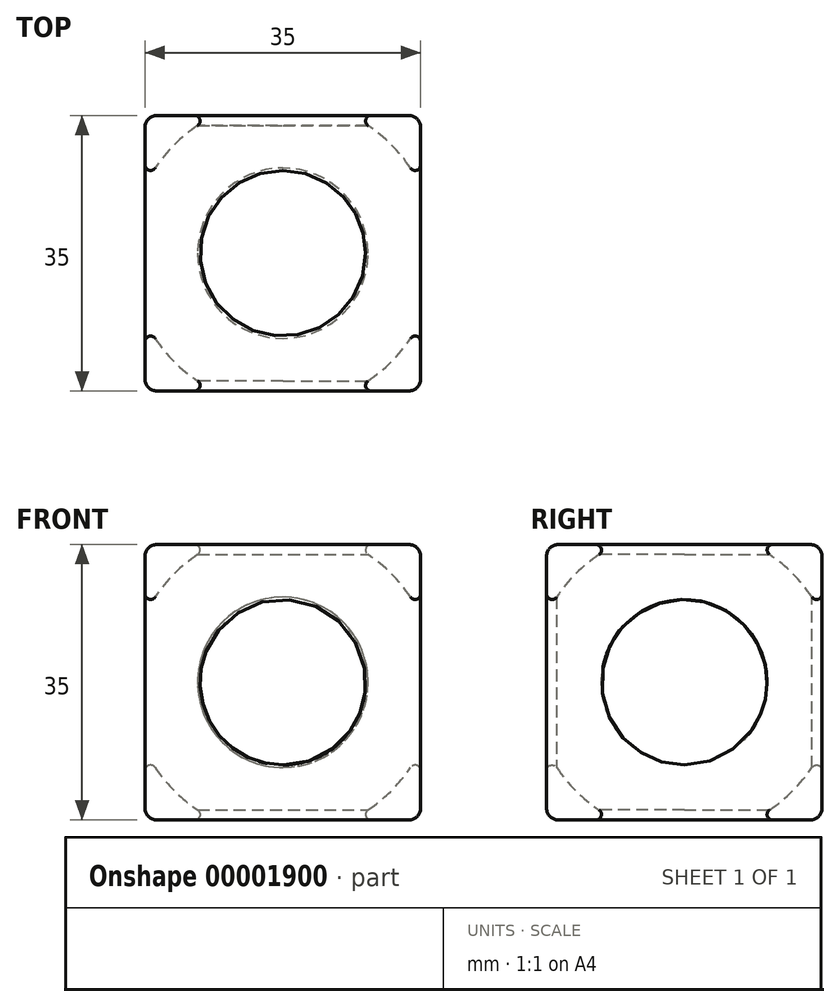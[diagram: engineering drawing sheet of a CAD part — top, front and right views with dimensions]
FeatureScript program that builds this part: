
annotation { "Feature Type Name" : "Feature", "Feature Type Description" : "" }
export const myFeature = defineFeature(function(context is Context, id is Id, definition is map)
    precondition{}
    {
        {
            var Q0;
            Q0=qCreatedBy(makeId("Top.planeOp"),FACE);
            var sketch = newSketch(context, id + "F0", { "sketchPlane" : qUnion([Q0])});
            skLineSegment(sketch, "E0.rect.bottom", {"start": v(10, 10) * mm, "end": v(-10, 10) * mm});
            skLineSegment(sketch, "E0.rect.top", {"start": v(10, -10) * mm, "end": v(-10, -10) * mm});
            skLineSegment(sketch, "E0.rect.left", {"start": v(10, 10) * mm, "end": v(10, -10) * mm});
            skLineSegment(sketch, "E0.rect.right", {"start": v(-10, 10) * mm, "end": v(-10, -10) * mm});
            skPoint(sketch, "E0.rect.middle", {"position": v(0, 0) * mm});
            skSolve(sketch);
        }
        {
            var Q0;
            Q0=qCreatedBy(makeId("Top.planeOp"),FACE);
            var sketch = newSketch(context, id + "F1", { "sketchPlane" : qUnion([Q0])});
            skArc(sketch, "E1", {"start": v(12, 0) * mm, "mid": v(0, 12) * mm, "end": v(-12, 0) * mm});
            skLineSegment(sketch, "E2", {"start": v(-12, 0) * mm, "end": v(12, 0) * mm});
            skSolve(sketch);
        }
        {
            var Q0;
            Q0=qCreatedBy(makeId("Top.planeOp"),FACE);
            var sketch = newSketch(context, id + "F2", { "sketchPlane" : qUnion([Q0])});
            skArc(sketch, "E3.0", {"start": v(14.8, 0) * mm, "mid": v(0, 14.8) * mm, "end": v(-14.8, 0) * mm});
            skArc(sketch, "E4.0", {"start": v(49.8, 0) * mm, "mid": v(0, 49.8) * mm, "end": v(-49.8, 0) * mm});
            skLineSegment(sketch, "E5", {"start": v(-49.8, 0) * mm, "end": v(-14.8, 0) * mm});
            skLineSegment(sketch, "E6", {"start": v(14.8, 0) * mm, "end": v(49.8, 0) * mm});
            skSolve(sketch);
        }
        {
            var Q0;
            Q0=makeQuery(id+"F0.imprint","IMPRINT",FACE,{"disambiguationData":[TD([[makeQuery(id+"F0.imprint","IMPRINT",EDGE,{"derivedFrom":sQuery(id+"F0.wireOp",EDGE,"E0.rect.bottom")}),1.0]])]});
            extrude(context, id + "F3", {"entities" : qUnion([Q0]), "endBound" : BoundingType.SYMMETRIC, "depth" : 20 * mm});
        }
        {
            var Q0;
            Q0=makeQuery(id+"F2.imprint","IMPRINT",FACE,{"disambiguationData":[TD([[makeQuery(id+"F2.imprint","IMPRINT",EDGE,{"derivedFrom":sQuery(id+"F2.wireOp",EDGE,"E3.0")}),-1.0]])]});
            var Q1;
            Q1=sQuery(id+"F2.wireOp",EDGE,"E5");
            revolve(context, id + "F4", {"operationType" : NewBodyOperationType.REMOVE, "entities" : qUnion([Q0]), "axis" : qUnion([Q1]), "revolveType" : RevolveType.FULL, "oppositeDirection" : true});
        }
        {
            var Q0;
            Q0=qSketchRegion(id+"F1",true);
            var Q1;
            Q1=sQuery(id+"F1.wireOp",EDGE,"E2");
            revolve(context, id + "F5", {"operationType" : NewBodyOperationType.REMOVE, "entities" : qUnion([Q0]), "axis" : qUnion([Q1]), "revolveType" : RevolveType.FULL, "oppositeDirection" : true});
        }
        {
            var Q0;
            Q0=qCreatedBy(makeId("Top.planeOp"),FACE);
            var sketch = newSketch(context, id + "F6", { "sketchPlane" : qUnion([Q0])});
            skArc(sketch, "E7.0", {"start": v(15.4, 0) * mm, "mid": v(0, 15.4) * mm, "end": v(-15.4, 0) * mm});
            skLineSegment(sketch, "E8", {"start": v(-15.4, 0) * mm, "end": v(15.4, 0) * mm});
            skLineSegment(sketch, "E9.rect.bottom", {"start": v(13.5, 13.5) * mm, "end": v(-13.5, 13.5) * mm});
            skLineSegment(sketch, "E9.rect.top", {"start": v(13.5, -13.5) * mm, "end": v(-13.5, -13.5) * mm});
            skLineSegment(sketch, "E9.rect.left", {"start": v(13.5, 13.5) * mm, "end": v(13.5, -13.5) * mm});
            skLineSegment(sketch, "E9.rect.right", {"start": v(-13.5, 13.5) * mm, "end": v(-13.5, -13.5) * mm});
            skArc(sketch, "E10.0", {"start": v(18.9, 0) * mm, "mid": v(0, 18.9) * mm, "end": v(-18.9, 0) * mm});
            skArc(sketch, "E11.0", {"start": v(33.9, 0) * mm, "mid": v(0, 33.9) * mm, "end": v(-33.9, 0) * mm});
            skLineSegment(sketch, "E12", {"start": v(-33.9, 0) * mm, "end": v(-18.9, 0) * mm});
            skLineSegment(sketch, "E13", {"start": v(18.9, 0) * mm, "end": v(33.9, 0) * mm});
            skSolve(sketch);
        }
        {
            var Q0;
            {var subQ1=sQuery(id+"F6.wireOp",EDGE,"E7.0");var subQ3=sQuery(id+"F6.wireOp",EDGE,"E9.rect.bottom");var subQ5=makeQuery(id+"F6.imprint","INTERSECT",VERTEX,{"disambiguationData":[OD(1.0)],"derivedFrom":[subQ1,subQ3]});Q0=makeQuery(id+"F6.imprint","IMPRINT",FACE,{"disambiguationData":[TD([[makeQuery(id+"F6.imprint","IMPRINT",EDGE,{"disambiguationData":[TD([[subQ5,-1.0]])],"derivedFrom":subQ1}),-1.0]])]});}
            var Q1;
            {var subQ3=sQuery(id+"F6.wireOp",EDGE,"E7.0");var subQ5=sQuery(id+"F6.wireOp",EDGE,"E9.rect.left");var subQ7=makeQuery(id+"F6.imprint","INTERSECT",VERTEX,{"derivedFrom":[subQ3,subQ5]});Q1=makeQuery(id+"F6.imprint","IMPRINT",FACE,{"disambiguationData":[TD([[makeQuery(id+"F6.imprint","IMPRINT",EDGE,{"disambiguationData":[TD([[subQ7,-1.0]])],"derivedFrom":subQ3}),1.0]])]});}
            var Q2;
            {var subQ0=sQuery(id+"F6.wireOp",EDGE,"E9.rect.left");var subQ1=sQuery(id+"F6.wireOp",EDGE,"E7.0");var subQ2=makeQuery(id+"F6.imprint","INTERSECT",VERTEX,{"derivedFrom":[subQ1,subQ0]});Q2=makeQuery(id+"F6.imprint","IMPRINT",FACE,{"disambiguationData":[TD([[makeQuery(id+"F6.imprint","IMPRINT",EDGE,{"disambiguationData":[TD([[subQ2,-1.0]])],"derivedFrom":subQ1}),-1.0]])]});}
            var Q3;
            {var subQ3=sQuery(id+"F6.wireOp",EDGE,"E9.rect.top");Q3=makeQuery(id+"F6.imprint","IMPRINT",FACE,{"disambiguationData":[TD([[makeQuery(id+"F6.imprint","IMPRINT",EDGE,{"derivedFrom":subQ3}),-1.0]])]});}
            var Q4;
            {var subQ0=sQuery(id+"F6.wireOp",EDGE,"E9.rect.left");var subQ3=sQuery(id+"F6.wireOp",EDGE,"E9.rect.bottom");var subQ4=makeQuery(id+"F6.imprint","INTERSECT",VERTEX,{"derivedFrom":[subQ3,subQ0]});Q4=makeQuery(id+"F6.imprint","IMPRINT",FACE,{"disambiguationData":[TD([[makeQuery(id+"F6.imprint","IMPRINT",EDGE,{"disambiguationData":[TD([[subQ4,-1.0]])],"derivedFrom":subQ3}),1.0]])]});}
            var Q5;
            {var subQ1=sQuery(id+"F6.wireOp",EDGE,"E9.rect.bottom");var subQ3=sQuery(id+"F6.wireOp",EDGE,"E9.rect.right");var subQ5=makeQuery(id+"F6.imprint","INTERSECT",VERTEX,{"derivedFrom":[subQ1,subQ3]});Q5=makeQuery(id+"F6.imprint","IMPRINT",FACE,{"disambiguationData":[TD([[makeQuery(id+"F6.imprint","IMPRINT",EDGE,{"disambiguationData":[TD([[subQ5,1.0]])],"derivedFrom":subQ1}),1.0]])]});}
            extrude(context, id + "F7", {"entities" : qUnion([Q0, Q1, Q2, Q3, Q4, Q5]), "endBound" : BoundingType.SYMMETRIC, "depth" : 27 * mm});
        }
        {
            var Q0;
            Q0=makeQuery(id+"F6.imprint","IMPRINT",FACE,{"disambiguationData":[TD([[makeQuery(id+"F6.imprint","IMPRINT",EDGE,{"derivedFrom":sQuery(id+"F6.wireOp",EDGE,"E11.0")}),1.0]])]});
            var Q1;
            {var subQ1=sQuery(id+"F6.wireOp",EDGE,"E9.rect.bottom");var subQ3=sQuery(id+"F6.wireOp",EDGE,"E9.rect.right");var subQ5=makeQuery(id+"F6.imprint","INTERSECT",VERTEX,{"derivedFrom":[subQ1,subQ3]});Q1=makeQuery(id+"F6.imprint","IMPRINT",FACE,{"disambiguationData":[TD([[makeQuery(id+"F6.imprint","IMPRINT",EDGE,{"disambiguationData":[TD([[subQ5,1.0]])],"derivedFrom":subQ1}),1.0]])]});}
            var Q2;
            {var subQ0=sQuery(id+"F6.wireOp",EDGE,"E9.rect.left");var subQ3=sQuery(id+"F6.wireOp",EDGE,"E9.rect.bottom");var subQ4=makeQuery(id+"F6.imprint","INTERSECT",VERTEX,{"derivedFrom":[subQ3,subQ0]});Q2=makeQuery(id+"F6.imprint","IMPRINT",FACE,{"disambiguationData":[TD([[makeQuery(id+"F6.imprint","IMPRINT",EDGE,{"disambiguationData":[TD([[subQ4,-1.0]])],"derivedFrom":subQ3}),1.0]])]});}
            var Q3;
            Q3=sQuery(id+"F6.wireOp",EDGE,"E12");
            revolve(context, id + "F8", {"operationType" : NewBodyOperationType.REMOVE, "entities" : qUnion([Q0, Q1, Q2]), "axis" : qUnion([Q3]), "revolveType" : RevolveType.FULL, "oppositeDirection" : true});
        }
        {
            var Q0;
            {var subQ1=sQuery(id+"F6.wireOp",EDGE,"E8");var subQ3=sQuery(id+"F6.wireOp",EDGE,"E7.0");var subQ5=makeQuery(id+"F6.imprint","INTERSECT",VERTEX,{"disambiguationData":[OD(1.0)],"derivedFrom":[subQ3,subQ1]});Q0=makeQuery(id+"F6.imprint","IMPRINT",FACE,{"disambiguationData":[TD([[makeQuery(id+"F6.imprint","IMPRINT",EDGE,{"disambiguationData":[TD([[subQ5,1.0]])],"derivedFrom":subQ3}),1.0]])]});}
            var Q1;
            {var subQ3=sQuery(id+"F6.wireOp",EDGE,"E7.0");var subQ5=sQuery(id+"F6.wireOp",EDGE,"E9.rect.left");var subQ7=makeQuery(id+"F6.imprint","INTERSECT",VERTEX,{"derivedFrom":[subQ3,subQ5]});Q1=makeQuery(id+"F6.imprint","IMPRINT",FACE,{"disambiguationData":[TD([[makeQuery(id+"F6.imprint","IMPRINT",EDGE,{"disambiguationData":[TD([[subQ7,-1.0]])],"derivedFrom":subQ3}),1.0]])]});}
            var Q2;
            {var subQ0=sQuery(id+"F6.wireOp",EDGE,"E9.rect.bottom");var subQ1=sQuery(id+"F6.wireOp",EDGE,"E7.0");var subQ3=makeQuery(id+"F6.imprint","INTERSECT",VERTEX,{"disambiguationData":[OD(0.0)],"derivedFrom":[subQ1,subQ0]});Q2=makeQuery(id+"F6.imprint","IMPRINT",FACE,{"disambiguationData":[TD([[makeQuery(id+"F6.imprint","IMPRINT",EDGE,{"disambiguationData":[TD([[subQ3,-1.0]])],"derivedFrom":subQ1}),1.0]])]});}
            var Q3;
            {var subQ1=sQuery(id+"F6.wireOp",EDGE,"E8");var subQ3=sQuery(id+"F6.wireOp",EDGE,"E7.0");var subQ5=makeQuery(id+"F6.imprint","INTERSECT",VERTEX,{"disambiguationData":[OD(0.0)],"derivedFrom":[subQ3,subQ1]});Q3=makeQuery(id+"F6.imprint","IMPRINT",FACE,{"disambiguationData":[TD([[makeQuery(id+"F6.imprint","IMPRINT",EDGE,{"disambiguationData":[TD([[subQ5,-1.0]])],"derivedFrom":subQ3}),1.0]])]});}
            var Q4;
            Q4=sQuery(id+"F6.wireOp",EDGE,"E8");
            revolve(context, id + "F9", {"operationType" : NewBodyOperationType.REMOVE, "entities" : qUnion([Q0, Q1, Q2, Q3]), "axis" : qUnion([Q4]), "revolveType" : RevolveType.FULL, "oppositeDirection" : true});
        }
        {
            var Q0;
            Q0=qCreatedBy(makeId("Top.planeOp"),FACE);
            var sketch = newSketch(context, id + "F10", { "sketchPlane" : qUnion([Q0])});
            skArc(sketch, "E14.0", {"start": v(19.5, 0) * mm, "mid": v(0, 19.5) * mm, "end": v(-19.5, 0) * mm});
            skLineSegment(sketch, "E15", {"start": v(-19.5, 0) * mm, "end": v(19.5, 0) * mm});
            skLineSegment(sketch, "E16.rect.bottom", {"start": v(17.5, 17.5) * mm, "end": v(-17.5, 17.5) * mm});
            skLineSegment(sketch, "E16.rect.top", {"start": v(17.5, -17.5) * mm, "end": v(-17.5, -17.5) * mm});
            skLineSegment(sketch, "E16.rect.left", {"start": v(17.5, 17.5) * mm, "end": v(17.5, -17.5) * mm});
            skLineSegment(sketch, "E16.rect.right", {"start": v(-17.5, 17.5) * mm, "end": v(-17.5, -17.5) * mm});
            skArc(sketch, "E17.0", {"start": v(23, 0) * mm, "mid": v(0, 23) * mm, "end": v(-23, 0) * mm});
            skArc(sketch, "E18.0", {"start": v(57.92, 0) * mm, "mid": v(0, 57.92) * mm, "end": v(-57.92, 0) * mm});
            skLineSegment(sketch, "E19", {"start": v(-57.92, 0) * mm, "end": v(-23, 0) * mm});
            skLineSegment(sketch, "E20", {"start": v(23, 0) * mm, "end": v(57.92, 0) * mm});
            skSolve(sketch);
        }
        {
            var Q0;
            {var subQ3=sQuery(id+"F10.wireOp",EDGE,"E16.rect.top");Q0=makeQuery(id+"F10.imprint","IMPRINT",FACE,{"disambiguationData":[TD([[makeQuery(id+"F10.imprint","IMPRINT",EDGE,{"derivedFrom":subQ3}),-1.0]])]});}
            var Q1;
            {var subQ3=sQuery(id+"F10.wireOp",EDGE,"E14.0");var subQ8=sQuery(id+"F10.wireOp",EDGE,"E16.rect.left");var subQ10=makeQuery(id+"F10.imprint","INTERSECT",VERTEX,{"derivedFrom":[subQ3,subQ8]});Q1=makeQuery(id+"F10.imprint","IMPRINT",FACE,{"disambiguationData":[TD([[makeQuery(id+"F10.imprint","IMPRINT",EDGE,{"disambiguationData":[TD([[subQ10,-1.0]])],"derivedFrom":subQ3}),1.0]])]});}
            var Q2;
            {var subQ1=sQuery(id+"F10.wireOp",EDGE,"E14.0");var subQ3=sQuery(id+"F10.wireOp",EDGE,"E16.rect.bottom");var subQ5=makeQuery(id+"F10.imprint","INTERSECT",VERTEX,{"disambiguationData":[OD(1.0)],"derivedFrom":[subQ1,subQ3]});Q2=makeQuery(id+"F10.imprint","IMPRINT",FACE,{"disambiguationData":[TD([[makeQuery(id+"F10.imprint","IMPRINT",EDGE,{"disambiguationData":[TD([[subQ5,-1.0]])],"derivedFrom":subQ1}),-1.0]])]});}
            var Q3;
            {var subQ0=sQuery(id+"F10.wireOp",EDGE,"E16.rect.left");var subQ1=sQuery(id+"F10.wireOp",EDGE,"E14.0");var subQ2=makeQuery(id+"F10.imprint","INTERSECT",VERTEX,{"derivedFrom":[subQ1,subQ0]});Q3=makeQuery(id+"F10.imprint","IMPRINT",FACE,{"disambiguationData":[TD([[makeQuery(id+"F10.imprint","IMPRINT",EDGE,{"disambiguationData":[TD([[subQ2,-1.0]])],"derivedFrom":subQ1}),-1.0]])]});}
            var Q4;
            {var subQ1=sQuery(id+"F10.wireOp",EDGE,"E16.rect.bottom");var subQ3=sQuery(id+"F10.wireOp",EDGE,"E16.rect.right");var subQ5=makeQuery(id+"F10.imprint","INTERSECT",VERTEX,{"derivedFrom":[subQ1,subQ3]});Q4=makeQuery(id+"F10.imprint","IMPRINT",FACE,{"disambiguationData":[TD([[makeQuery(id+"F10.imprint","IMPRINT",EDGE,{"disambiguationData":[TD([[subQ5,1.0]])],"derivedFrom":subQ1}),1.0]])]});}
            var Q5;
            {var subQ1=sQuery(id+"F10.wireOp",EDGE,"E16.rect.bottom");var subQ3=sQuery(id+"F10.wireOp",EDGE,"E16.rect.left");var subQ5=makeQuery(id+"F10.imprint","INTERSECT",VERTEX,{"derivedFrom":[subQ1,subQ3]});Q5=makeQuery(id+"F10.imprint","IMPRINT",FACE,{"disambiguationData":[TD([[makeQuery(id+"F10.imprint","IMPRINT",EDGE,{"disambiguationData":[TD([[subQ5,-1.0]])],"derivedFrom":subQ1}),1.0]])]});}
            extrude(context, id + "F11", {"entities" : qUnion([Q0, Q1, Q2, Q3, Q4, Q5]), "endBound" : BoundingType.SYMMETRIC, "depth" : 35 * mm});
        }
        {
            var Q0;
            {var subQ3=sQuery(id+"F10.wireOp",EDGE,"E14.0");var subQ8=sQuery(id+"F10.wireOp",EDGE,"E16.rect.left");var subQ10=makeQuery(id+"F10.imprint","INTERSECT",VERTEX,{"derivedFrom":[subQ3,subQ8]});Q0=makeQuery(id+"F10.imprint","IMPRINT",FACE,{"disambiguationData":[TD([[makeQuery(id+"F10.imprint","IMPRINT",EDGE,{"disambiguationData":[TD([[subQ10,-1.0]])],"derivedFrom":subQ3}),1.0]])]});}
            var Q1;
            {var subQ1=sQuery(id+"F10.wireOp",EDGE,"E15");var subQ3=sQuery(id+"F10.wireOp",EDGE,"E14.0");var subQ5=makeQuery(id+"F10.imprint","INTERSECT",VERTEX,{"disambiguationData":[OD(1.0)],"derivedFrom":[subQ3,subQ1]});Q1=makeQuery(id+"F10.imprint","IMPRINT",FACE,{"disambiguationData":[TD([[makeQuery(id+"F10.imprint","IMPRINT",EDGE,{"disambiguationData":[TD([[subQ5,1.0]])],"derivedFrom":subQ3}),1.0]])]});}
            var Q2;
            {var subQ1=sQuery(id+"F10.wireOp",EDGE,"E15");var subQ3=sQuery(id+"F10.wireOp",EDGE,"E14.0");var subQ5=makeQuery(id+"F10.imprint","INTERSECT",VERTEX,{"disambiguationData":[OD(0.0)],"derivedFrom":[subQ3,subQ1]});Q2=makeQuery(id+"F10.imprint","IMPRINT",FACE,{"disambiguationData":[TD([[makeQuery(id+"F10.imprint","IMPRINT",EDGE,{"disambiguationData":[TD([[subQ5,-1.0]])],"derivedFrom":subQ3}),1.0]])]});}
            var Q3;
            {var subQ0=sQuery(id+"F10.wireOp",EDGE,"E16.rect.bottom");var subQ1=sQuery(id+"F10.wireOp",EDGE,"E14.0");var subQ3=makeQuery(id+"F10.imprint","INTERSECT",VERTEX,{"disambiguationData":[OD(0.0)],"derivedFrom":[subQ1,subQ0]});Q3=makeQuery(id+"F10.imprint","IMPRINT",FACE,{"disambiguationData":[TD([[makeQuery(id+"F10.imprint","IMPRINT",EDGE,{"disambiguationData":[TD([[subQ3,-1.0]])],"derivedFrom":subQ1}),1.0]])]});}
            var Q4;
            Q4=sQuery(id+"F10.wireOp",EDGE,"E15");
            revolve(context, id + "F12", {"operationType" : NewBodyOperationType.REMOVE, "entities" : qUnion([Q0, Q1, Q2, Q3]), "axis" : qUnion([Q4]), "revolveType" : RevolveType.FULL, "oppositeDirection" : true});
        }
        {
            var Q0;
            Q0=makeQuery(id+"F12.boolean.opBoolean","INTERSECT",EDGE,{"derivedFrom":[makeQuery(id+"F11.opExtrude","CAP_FACE",FACE,{"disambiguationData":[OSD([sQuery(id+"F10.wireOp",EDGE,"E16.rect.bottom"),sQuery(id+"F10.wireOp",EDGE,"E16.rect.top"),sQuery(id+"F10.wireOp",EDGE,"E16.rect.left"),sQuery(id+"F10.wireOp",EDGE,"E16.rect.right")])],"isStart":false}),makeQuery(id+"F12.opRevolve","SWEPT_FACE",FACE,{"disambiguationData":[OSD([sQuery(id+"F10.wireOp",EDGE,"E14.0")])]})]});
            var Q1;
            Q1=makeQuery(id+"F9.boolean.opBoolean","INTERSECT",EDGE,{"derivedFrom":[makeQuery(id+"F7.opExtrude","CAP_FACE",FACE,{"disambiguationData":[OSD([sQuery(id+"F6.wireOp",EDGE,"E9.rect.bottom"),sQuery(id+"F6.wireOp",EDGE,"E9.rect.top"),sQuery(id+"F6.wireOp",EDGE,"E9.rect.left"),sQuery(id+"F6.wireOp",EDGE,"E9.rect.right")])],"isStart":false}),makeQuery(id+"F9.opRevolve","SWEPT_FACE",FACE,{"disambiguationData":[OSD([sQuery(id+"F6.wireOp",EDGE,"E7.0")])]})]});
            var Q2;
            Q2=makeQuery(id+"F12.boolean.opBoolean","INTERSECT",EDGE,{"derivedFrom":[makeQuery(id+"F11.opExtrude","SWEPT_FACE",FACE,{"disambiguationData":[OSD([sQuery(id+"F10.wireOp",EDGE,"E16.rect.top")])]}),makeQuery(id+"F12.opRevolve","SWEPT_FACE",FACE,{"disambiguationData":[OSD([sQuery(id+"F10.wireOp",EDGE,"E14.0")])]})]});
            var Q3;
            Q3=makeQuery(id+"F9.boolean.opBoolean","INTERSECT",EDGE,{"derivedFrom":[makeQuery(id+"F7.opExtrude","SWEPT_FACE",FACE,{"disambiguationData":[OSD([sQuery(id+"F6.wireOp",EDGE,"E9.rect.top")])]}),makeQuery(id+"F9.opRevolve","SWEPT_FACE",FACE,{"disambiguationData":[OSD([sQuery(id+"F6.wireOp",EDGE,"E7.0")])]})]});
            var Q4;
            Q4=makeQuery(id+"F9.boolean.opBoolean","INTERSECT",EDGE,{"derivedFrom":[makeQuery(id+"F7.opExtrude","SWEPT_FACE",FACE,{"disambiguationData":[OSD([sQuery(id+"F6.wireOp",EDGE,"E9.rect.left")])]}),makeQuery(id+"F9.opRevolve","SWEPT_FACE",FACE,{"disambiguationData":[OSD([sQuery(id+"F6.wireOp",EDGE,"E7.0")])]})]});
            var Q5;
            Q5=makeQuery(id+"F12.boolean.opBoolean","INTERSECT",EDGE,{"derivedFrom":[makeQuery(id+"F11.opExtrude","SWEPT_FACE",FACE,{"disambiguationData":[OSD([sQuery(id+"F10.wireOp",EDGE,"E16.rect.left")])]}),makeQuery(id+"F12.opRevolve","SWEPT_FACE",FACE,{"disambiguationData":[OSD([sQuery(id+"F10.wireOp",EDGE,"E14.0")])]})]});
            var Q6;
            Q6=makeQuery(id+"F9.boolean.opBoolean","INTERSECT",EDGE,{"derivedFrom":[makeQuery(id+"F7.opExtrude","SWEPT_FACE",FACE,{"disambiguationData":[OSD([sQuery(id+"F6.wireOp",EDGE,"E9.rect.bottom")])]}),makeQuery(id+"F9.opRevolve","SWEPT_FACE",FACE,{"disambiguationData":[OSD([sQuery(id+"F6.wireOp",EDGE,"E7.0")])]})]});
            var Q7;
            Q7=makeQuery(id+"F12.boolean.opBoolean","INTERSECT",EDGE,{"derivedFrom":[makeQuery(id+"F11.opExtrude","SWEPT_FACE",FACE,{"disambiguationData":[OSD([sQuery(id+"F10.wireOp",EDGE,"E16.rect.bottom")])]}),makeQuery(id+"F12.opRevolve","SWEPT_FACE",FACE,{"disambiguationData":[OSD([sQuery(id+"F10.wireOp",EDGE,"E14.0")])]})]});
            var Q8;
            Q8=makeQuery(id+"F9.boolean.opBoolean","INTERSECT",EDGE,{"derivedFrom":[makeQuery(id+"F7.opExtrude","CAP_FACE",FACE,{"disambiguationData":[OSD([sQuery(id+"F6.wireOp",EDGE,"E9.rect.bottom"),sQuery(id+"F6.wireOp",EDGE,"E9.rect.top"),sQuery(id+"F6.wireOp",EDGE,"E9.rect.left"),sQuery(id+"F6.wireOp",EDGE,"E9.rect.right")])],"isStart":true}),makeQuery(id+"F9.opRevolve","SWEPT_FACE",FACE,{"disambiguationData":[OSD([sQuery(id+"F6.wireOp",EDGE,"E7.0")])]})]});
            var Q9;
            Q9=makeQuery(id+"F12.boolean.opBoolean","INTERSECT",EDGE,{"derivedFrom":[makeQuery(id+"F11.opExtrude","CAP_FACE",FACE,{"disambiguationData":[OSD([sQuery(id+"F10.wireOp",EDGE,"E16.rect.bottom"),sQuery(id+"F10.wireOp",EDGE,"E16.rect.top"),sQuery(id+"F10.wireOp",EDGE,"E16.rect.left"),sQuery(id+"F10.wireOp",EDGE,"E16.rect.right")])],"isStart":true}),makeQuery(id+"F12.opRevolve","SWEPT_FACE",FACE,{"disambiguationData":[OSD([sQuery(id+"F10.wireOp",EDGE,"E14.0")])]})]});
            var Q10;
            Q10=makeQuery(id+"F9.boolean.opBoolean","INTERSECT",EDGE,{"derivedFrom":[makeQuery(id+"F7.opExtrude","SWEPT_FACE",FACE,{"disambiguationData":[OSD([sQuery(id+"F6.wireOp",EDGE,"E9.rect.right")])]}),makeQuery(id+"F9.opRevolve","SWEPT_FACE",FACE,{"disambiguationData":[OSD([sQuery(id+"F6.wireOp",EDGE,"E7.0")])]})]});
            var Q11;
            Q11=makeQuery(id+"F12.boolean.opBoolean","INTERSECT",EDGE,{"derivedFrom":[makeQuery(id+"F11.opExtrude","SWEPT_FACE",FACE,{"disambiguationData":[OSD([sQuery(id+"F10.wireOp",EDGE,"E16.rect.right")])]}),makeQuery(id+"F12.opRevolve","SWEPT_FACE",FACE,{"disambiguationData":[OSD([sQuery(id+"F10.wireOp",EDGE,"E14.0")])]})]});
            var Q12;
            Q12=makeQuery(id+"F5.boolean.opBoolean","INTERSECT",EDGE,{"derivedFrom":[makeQuery(id+"F3.opExtrude","SWEPT_FACE",FACE,{"disambiguationData":[OSD([sQuery(id+"F0.wireOp",EDGE,"E0.rect.bottom")])]}),makeQuery(id+"F5.opRevolve","SWEPT_FACE",FACE,{"disambiguationData":[OSD([sQuery(id+"F1.wireOp",EDGE,"E1")])]})]});
            var Q13;
            Q13=makeQuery(id+"F5.boolean.opBoolean","INTERSECT",EDGE,{"derivedFrom":[makeQuery(id+"F3.opExtrude","SWEPT_FACE",FACE,{"disambiguationData":[OSD([sQuery(id+"F0.wireOp",EDGE,"E0.rect.right")])]}),makeQuery(id+"F5.opRevolve","SWEPT_FACE",FACE,{"disambiguationData":[OSD([sQuery(id+"F1.wireOp",EDGE,"E1")])]})]});
            var Q14;
            Q14=makeQuery(id+"F5.boolean.opBoolean","INTERSECT",EDGE,{"derivedFrom":[makeQuery(id+"F3.opExtrude","CAP_FACE",FACE,{"disambiguationData":[OSD([sQuery(id+"F0.wireOp",EDGE,"E0.rect.bottom"),sQuery(id+"F0.wireOp",EDGE,"E0.rect.top"),sQuery(id+"F0.wireOp",EDGE,"E0.rect.left"),sQuery(id+"F0.wireOp",EDGE,"E0.rect.right")])],"isStart":false}),makeQuery(id+"F5.opRevolve","SWEPT_FACE",FACE,{"disambiguationData":[OSD([sQuery(id+"F1.wireOp",EDGE,"E1")])]})]});
            var Q15;
            Q15=makeQuery(id+"F5.boolean.opBoolean","INTERSECT",EDGE,{"derivedFrom":[makeQuery(id+"F3.opExtrude","SWEPT_FACE",FACE,{"disambiguationData":[OSD([sQuery(id+"F0.wireOp",EDGE,"E0.rect.left")])]}),makeQuery(id+"F5.opRevolve","SWEPT_FACE",FACE,{"disambiguationData":[OSD([sQuery(id+"F1.wireOp",EDGE,"E1")])]})]});
            var Q16;
            Q16=makeQuery(id+"F5.boolean.opBoolean","INTERSECT",EDGE,{"derivedFrom":[makeQuery(id+"F3.opExtrude","CAP_FACE",FACE,{"disambiguationData":[OSD([sQuery(id+"F0.wireOp",EDGE,"E0.rect.bottom"),sQuery(id+"F0.wireOp",EDGE,"E0.rect.top"),sQuery(id+"F0.wireOp",EDGE,"E0.rect.left"),sQuery(id+"F0.wireOp",EDGE,"E0.rect.right")])],"isStart":true}),makeQuery(id+"F5.opRevolve","SWEPT_FACE",FACE,{"disambiguationData":[OSD([sQuery(id+"F1.wireOp",EDGE,"E1")])]})]});
            var Q17;
            Q17=makeQuery(id+"F5.boolean.opBoolean","INTERSECT",EDGE,{"derivedFrom":[makeQuery(id+"F3.opExtrude","SWEPT_FACE",FACE,{"disambiguationData":[OSD([sQuery(id+"F0.wireOp",EDGE,"E0.rect.top")])]}),makeQuery(id+"F5.opRevolve","SWEPT_FACE",FACE,{"disambiguationData":[OSD([sQuery(id+"F1.wireOp",EDGE,"E1")])]})]});
            fillet(context, id + "F13", {"entities" : qUnion([Q0, Q1, Q2, Q3, Q4, Q5, Q6, Q7, Q8, Q9, Q10, Q11, Q12, Q13, Q14, Q15, Q16, Q17]), "radius" : .7 * mm, "tangentPropagation" : true, "allowEdgeOverflow" : false});
        }
        {
            var Q0;
            Q0=makeQuery(id+"F11.opExtrude","CAP_EDGE",EDGE,{"disambiguationData":[OSD([sQuery(id+"F10.wireOp",EDGE,"E16.rect.right")])],"isStart":false});
            var Q1;
            Q1=makeQuery(id+"F11.opExtrude","CAP_EDGE",EDGE,{"disambiguationData":[OSD([sQuery(id+"F10.wireOp",EDGE,"E16.rect.top")])],"isStart":false});
            var Q2;
            Q2=makeQuery(id+"F11.opExtrude","SWEPT_EDGE",EDGE,{"disambiguationData":[OSD([sQuery(id+"F10.wireOp",EDGE,"E16.rect.top"),sQuery(id+"F10.wireOp",EDGE,"E16.rect.right")])]});
            var Q3;
            Q3=makeQuery(id+"F11.opExtrude","SWEPT_EDGE",EDGE,{"disambiguationData":[OSD([sQuery(id+"F10.wireOp",EDGE,"E16.rect.bottom"),sQuery(id+"F10.wireOp",EDGE,"E16.rect.right")])]});
            var Q4;
            Q4=makeQuery(id+"F11.opExtrude","CAP_EDGE",EDGE,{"disambiguationData":[OSD([sQuery(id+"F10.wireOp",EDGE,"E16.rect.bottom")])],"isStart":false});
            var Q5;
            Q5=makeQuery(id+"F11.opExtrude","CAP_EDGE",EDGE,{"disambiguationData":[OSD([sQuery(id+"F10.wireOp",EDGE,"E16.rect.left")])],"isStart":false});
            var Q6;
            Q6=makeQuery(id+"F11.opExtrude","SWEPT_EDGE",EDGE,{"disambiguationData":[OSD([sQuery(id+"F10.wireOp",EDGE,"E16.rect.top"),sQuery(id+"F10.wireOp",EDGE,"E16.rect.left")])]});
            var Q7;
            Q7=makeQuery(id+"F11.opExtrude","CAP_EDGE",EDGE,{"disambiguationData":[OSD([sQuery(id+"F10.wireOp",EDGE,"E16.rect.left")])],"isStart":true});
            var Q8;
            Q8=makeQuery(id+"F11.opExtrude","CAP_EDGE",EDGE,{"disambiguationData":[OSD([sQuery(id+"F10.wireOp",EDGE,"E16.rect.top")])],"isStart":true});
            var Q9;
            Q9=makeQuery(id+"F11.opExtrude","SWEPT_EDGE",EDGE,{"disambiguationData":[OSD([sQuery(id+"F10.wireOp",EDGE,"E16.rect.bottom"),sQuery(id+"F10.wireOp",EDGE,"E16.rect.left")])]});
            var Q10;
            Q10=makeQuery(id+"F11.opExtrude","CAP_EDGE",EDGE,{"disambiguationData":[OSD([sQuery(id+"F10.wireOp",EDGE,"E16.rect.bottom")])],"isStart":true});
            var Q11;
            Q11=makeQuery(id+"F11.opExtrude","CAP_EDGE",EDGE,{"disambiguationData":[OSD([sQuery(id+"F10.wireOp",EDGE,"E16.rect.right")])],"isStart":true});
            fillet(context, id + "F14", {"entities" : qUnion([Q0, Q1, Q2, Q3, Q4, Q5, Q6, Q7, Q8, Q9, Q10, Q11]), "radius" : 1.5 * mm, "tangentPropagation" : true, "allowEdgeOverflow" : false});
        }
    });
